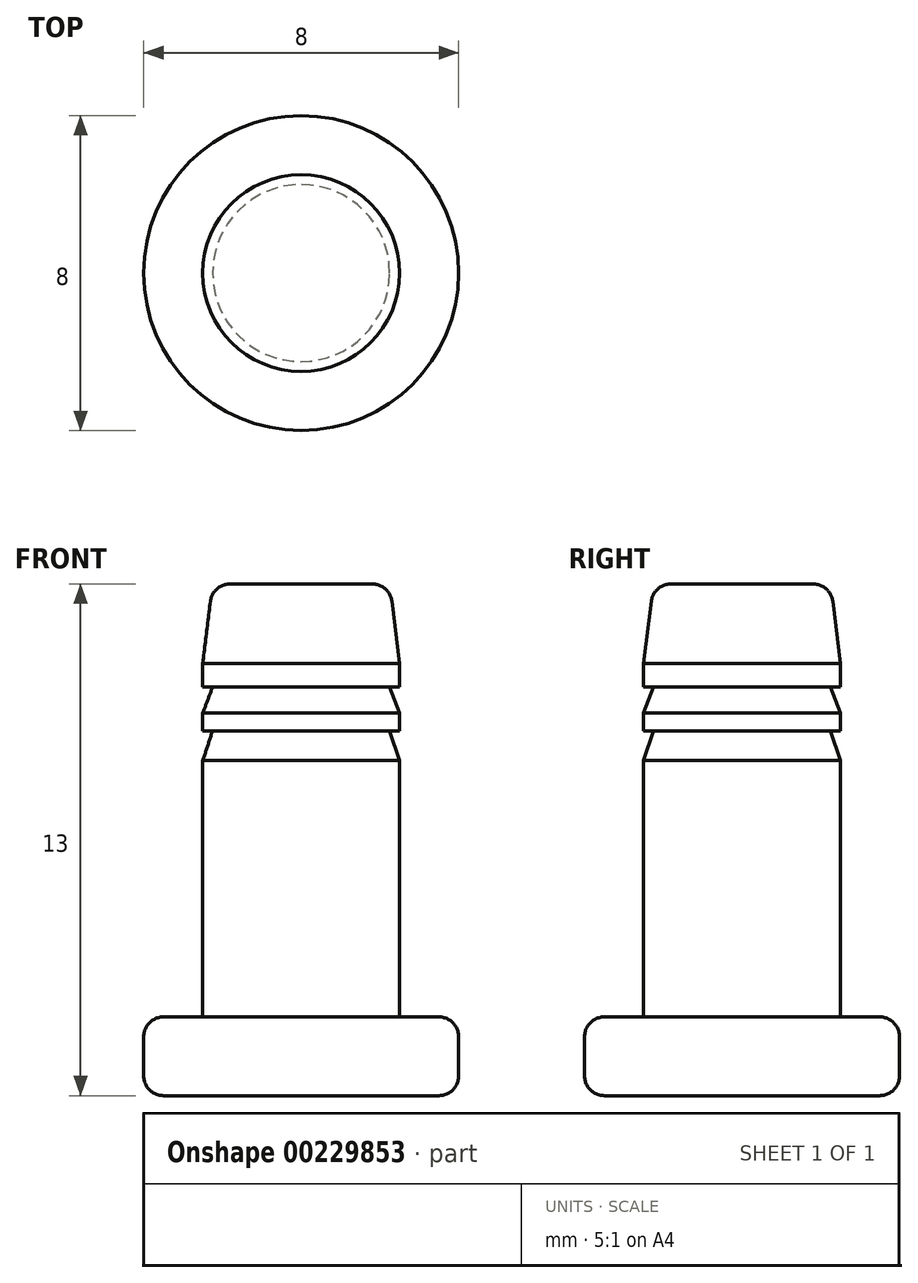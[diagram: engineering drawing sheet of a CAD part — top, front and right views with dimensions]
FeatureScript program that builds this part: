
annotation { "Feature Type Name" : "Feature", "Feature Type Description" : "" }
export const myFeature = defineFeature(function(context is Context, id is Id, definition is map)
    precondition{}
    {
        {
            var Q0;
            Q0=qCreatedBy(makeId("Front.planeOp"),FACE);
            var sketch = newSketch(context, id + "F0", { "sketchPlane" : qUnion([Q0])});
            skLineSegment(sketch, "E0", {"start": v(0, -23.64) * mm, "end": v(0, 30.17) * mm, "construction": true});
            skLineSegment(sketch, "E1", {"start": v(0, -2.35) * mm, "end": v(-4, -2.35) * mm});
            skLineSegment(sketch, "E2", {"start": v(-4, -2.35) * mm, "end": v(-4, -0.35) * mm});
            skLineSegment(sketch, "E3", {"start": v(-4, -0.35) * mm, "end": v(-2.5, -0.35) * mm});
            skLineSegment(sketch, "E4", {"start": v(-2.5, -0.35) * mm, "end": v(-2.5, 6.16) * mm});
            skLineSegment(sketch, "E5", {"start": v(-2.5, 6.16) * mm, "end": v(-2.25, 6.92) * mm});
            skLineSegment(sketch, "E6", {"start": v(-2.25, 6.92) * mm, "end": v(-2.5, 6.92) * mm});
            skLineSegment(sketch, "E7", {"start": v(-2.5, 6.92) * mm, "end": v(-2.5, 7.37) * mm});
            skLineSegment(sketch, "E8", {"start": v(-2.5, 7.37) * mm, "end": v(-2.25, 8.03) * mm});
            skLineSegment(sketch, "E9", {"start": v(-2.25, 8.03) * mm, "end": v(-2.5, 8.03) * mm});
            skLineSegment(sketch, "E10", {"start": v(-2.5, 8.03) * mm, "end": v(-2.5, 8.63) * mm});
            skLineSegment(sketch, "E11", {"start": v(-2.5, 8.63) * mm, "end": v(-2.25, 10.65) * mm});
            skLineSegment(sketch, "E12", {"start": v(-2.25, 10.65) * mm, "end": v(0, 10.65) * mm});
            skLineSegment(sketch, "E13", {"start": v(0, 10.65) * mm, "end": v(0, -2.35) * mm});
            skSolve(sketch);
        }
        {
            var Q0;
            Q0 = qSketchRegion(id + "F0", true);
            var Q1;
            Q1=sQuery(id+"F0.wireOp",EDGE,"E0");
            revolve(context, id + "F1", {"entities" : qUnion([Q0]), "axis" : qUnion([Q1]), "revolveType" : RevolveType.FULL});
        }
        {
            var Q0;
            Q0=makeQuery(id+"F1.opRevolve","SWEPT_EDGE",EDGE,{"disambiguationData":[OSD([sQuery(id+"F0.wireOp",EDGE,"E1"),sQuery(id+"F0.wireOp",EDGE,"E2")])]});
            fillet(context, id + "F2", {"entities" : qUnion([Q0]), "radius" : .5 * mm, "tangentPropagation" : true, "allowEdgeOverflow" : false});
        }
        {
            var Q0;
            Q0=makeQuery(id+"F1.opRevolve","SWEPT_EDGE",EDGE,{"disambiguationData":[OSD([sQuery(id+"F0.wireOp",EDGE,"E11"),sQuery(id+"F0.wireOp",EDGE,"E12")])]});
            var Q1;
            Q1=makeQuery(id+"F1.opRevolve","SWEPT_EDGE",EDGE,{"disambiguationData":[OSD([sQuery(id+"F0.wireOp",EDGE,"E2"),sQuery(id+"F0.wireOp",EDGE,"E3")])]});
            fillet(context, id + "F3", {"entities" : qUnion([Q0, Q1]), "radius" : .5 * mm, "tangentPropagation" : true, "allowEdgeOverflow" : false});
        }
    });
